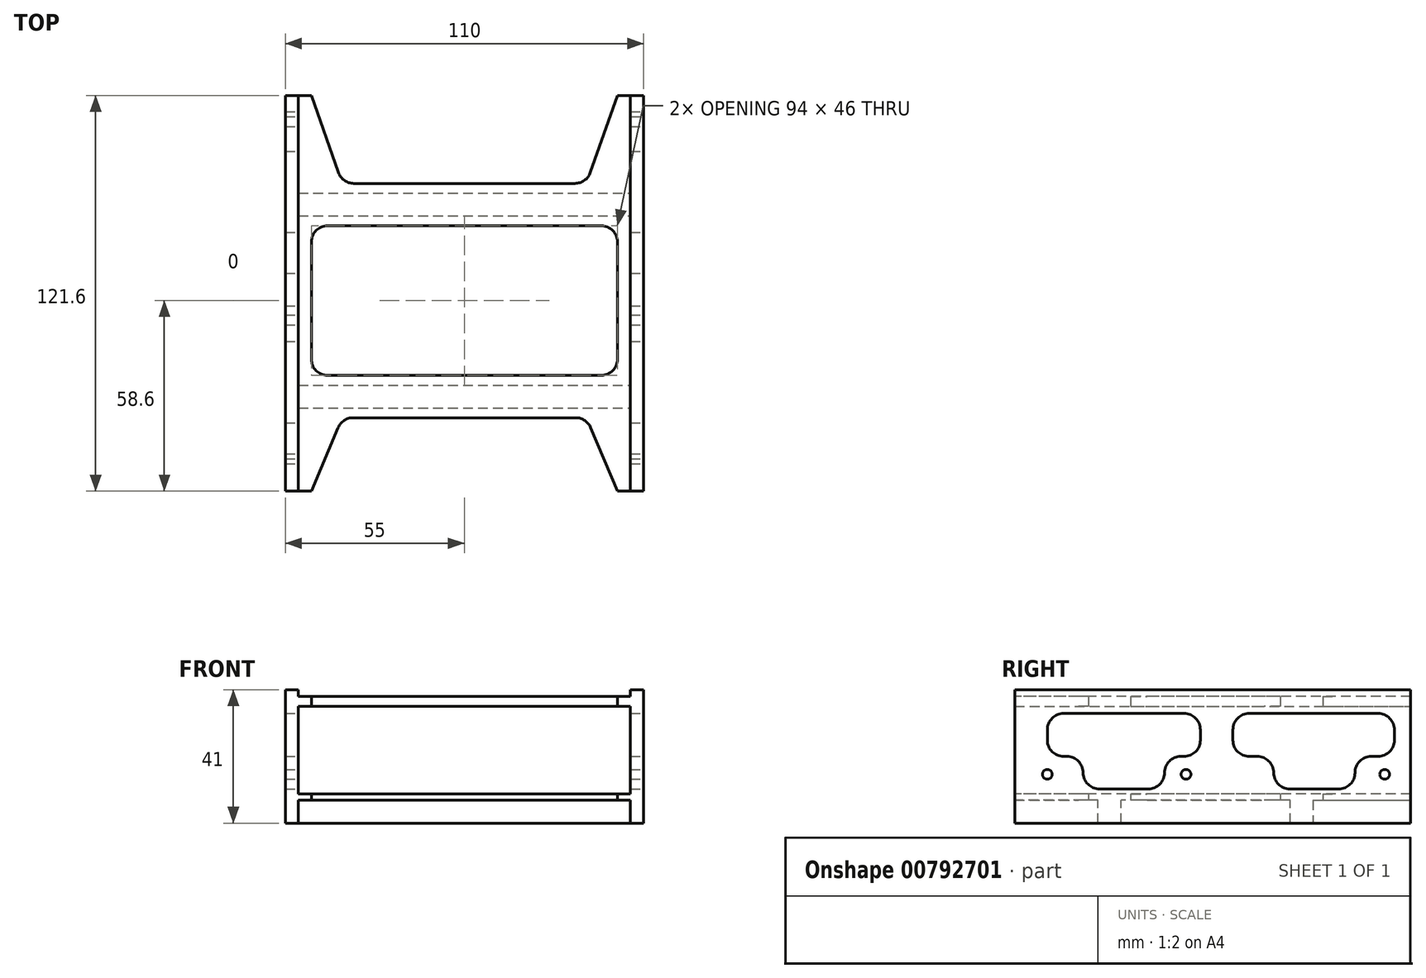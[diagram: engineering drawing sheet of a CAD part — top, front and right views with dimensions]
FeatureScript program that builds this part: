
annotation { "Feature Type Name" : "Feature", "Feature Type Description" : "" }
export const myFeature = defineFeature(function(context is Context, id is Id, definition is map)
    precondition{}
    {
        {
            var Q0;
            Q0=qCreatedBy(makeId("Right.planeOp"),FACE);
            var sketch = newSketch(context, id + "F0", { "sketchPlane" : qUnion([Q0])});
            skLineSegment(sketch, "E0.bottom", {"start": v(0, 0) * mm, "end": v(121.6, 0) * mm});
            skLineSegment(sketch, "E0.top", {"start": v(0, 41) * mm, "end": v(121.6, 41) * mm});
            skLineSegment(sketch, "E0.left", {"start": v(0, 0) * mm, "end": v(0, 41) * mm});
            skLineSegment(sketch, "E0.right", {"start": v(121.6, 0) * mm, "end": v(121.6, 41) * mm});
            skCircle(sketch, "E1", {"center": v(10, 15) * mm, "radius": 1.5 * mm});
            skCircle(sketch, "E2", {"center": v(52.6, 15) * mm, "radius": 1.5 * mm});
            skCircle(sketch, "E3", {"center": v(113.6, 15) * mm, "radius": 1.5 * mm});
            skLineSegment(sketch, "E4.bottom", {"start": v(-18.2, 35.2) * mm, "end": v(127.8, 35.2) * mm, "construction": true});
            skLineSegment(sketch, "E4.top", {"start": v(-18.2, 9.5) * mm, "end": v(127.8, 9.5) * mm, "construction": true});
            skLineSegment(sketch, "E4.left", {"start": v(-18.2, 35.2) * mm, "end": v(-18.2, 9.5) * mm, "construction": true});
            skLineSegment(sketch, "E4.right", {"start": v(127.8, 35.2) * mm, "end": v(127.8, 9.5) * mm, "construction": true});
            skSolve(sketch);
        }
        {
            var Q0;
            Q0=makeQuery(id+"F0.imprint","IMPRINT",FACE,{"disambiguationData":[TD([[makeQuery(id+"F0.imprint","IMPRINT",EDGE,{"derivedFrom":sQuery(id+"F0.wireOp",EDGE,"E0.bottom")}),1.0]])]});
            extrude(context, id + "F1", {"entities" : qUnion([Q0]), "oppositeDirection" : true, "depth" : 4 * mm, "offsetDistance" : 25 * mm});
        }
        {
            var Q0;
            Q0=makeQuery(id+"F1.opExtrude","CAP_FACE",FACE,{"disambiguationData":[OSD([sQuery(id+"F0.wireOp",EDGE,"E0.bottom"),sQuery(id+"F0.wireOp",EDGE,"E0.top"),sQuery(id+"F0.wireOp",EDGE,"E0.left"),sQuery(id+"F0.wireOp",EDGE,"E0.right"),sQuery(id+"F0.wireOp",EDGE,"E1"),sQuery(id+"F0.wireOp",EDGE,"E2"),sQuery(id+"F0.wireOp",EDGE,"E3")])],"isStart":false});
            var sketch = newSketch(context, id + "F2", { "sketchPlane" : qUnion([Q0])});
            skLineSegment(sketch, "E5.0", {"start": v(-127.8, 35.2) * mm, "end": v(-127.8, 9.5) * mm, "construction": true});
            skLineSegment(sketch, "E6.0", {"start": v(18.2, 35.2) * mm, "end": v(-127.8, 35.2) * mm, "construction": true});
            skLineSegment(sketch, "E7.0", {"start": v(18.2, 9.5) * mm, "end": v(-127.8, 9.5) * mm, "construction": true});
            skLineSegment(sketch, "E8.0", {"start": v(18.2, 35.2) * mm, "end": v(18.2, 9.5) * mm, "construction": true});
            skLineSegment(sketch, "E9.top", {"start": v(0, 35.95) * mm, "end": v(-121.6, 35.95) * mm});
            skLineSegment(sketch, "E9.left", {"start": v(0, 38.95) * mm, "end": v(0, 35.95) * mm});
            skLineSegment(sketch, "E9.right", {"start": v(-121.6, 38.95) * mm, "end": v(-121.6, 35.95) * mm});
            skLineSegment(sketch, "E10.top", {"start": v(-121.6, 9) * mm, "end": v(0, 9) * mm});
            skLineSegment(sketch, "E10.left", {"start": v(-121.6, 7) * mm, "end": v(-121.6, 9) * mm});
            skLineSegment(sketch, "E10.right", {"start": v(0, 7) * mm, "end": v(0, 9) * mm});
            skLineSegment(sketch, "E11", {"start": v(-91.6, 7) * mm, "end": v(-91.6, 0) * mm});
            skLineSegment(sketch, "E12", {"start": v(-91.6, 0) * mm, "end": v(-84.6, 0) * mm});
            skLineSegment(sketch, "E13", {"start": v(-84.6, 0) * mm, "end": v(-84.6, 7) * mm});
            skLineSegment(sketch, "E14", {"start": v(-32.6, 0) * mm, "end": v(-32.6, 7) * mm});
            skLineSegment(sketch, "E15", {"start": v(-25.6, 0) * mm, "end": v(-25.6, 7) * mm});
            skLineSegment(sketch, "E16", {"start": v(-32.6, 0) * mm, "end": v(-25.6, 0) * mm});
            skLineSegment(sketch, "E17.trimOffspring", {"start": v(-84.6, 7) * mm, "end": v(-32.6, 7) * mm});
            skLineSegment(sketch, "E18.trimOffspring", {"start": v(-25.6, 7) * mm, "end": v(0, 7) * mm});
            skLineSegment(sketch, "E19", {"start": v(-91.6, 7) * mm, "end": v(-121.6, 7) * mm});
            skLineSegment(sketch, "E20", {"start": v(-121.6, 38.95) * mm, "end": v(0, 38.95) * mm});
            skSolve(sketch);
        }
        {
            var Q0;
            Q0=makeQuery(id+"F2.imprint","IMPRINT",FACE,{"disambiguationData":[TD([[makeQuery(id+"F2.imprint","IMPRINT",EDGE,{"derivedFrom":sQuery(id+"F2.wireOp",EDGE,"E10.top")}),-1.0]])]});
            var Q1;
            Q1=makeQuery(id+"F2.imprint","IMPRINT",FACE,{"disambiguationData":[TD([[makeQuery(id+"F2.imprint","IMPRINT",EDGE,{"derivedFrom":sQuery(id+"F2.wireOp",EDGE,"E9.top")}),-1.0]])]});
            extrude(context, id + "F3", {"entities" : qUnion([Q0, Q1]), "operationType" : NewBodyOperationType.ADD, "depth" : 102 * mm, "offsetDistance" : 25 * mm});
        }
        {
            var Q0;
            Q0=makeQuery(id+"F3.opExtrude","SWEPT_FACE",FACE,{"disambiguationData":[OSD([sQuery(id+"F2.wireOp",EDGE,"E17.trimOffspring")])]});
            var sketch = newSketch(context, id + "F4", { "sketchPlane" : qUnion([Q0])});
            skLineSegment(sketch, "E21.0", {"start": v(-102, 0) * mm, "end": v(-8, 0) * mm});
            skLineSegment(sketch, "E22", {"start": v(-55, 0) * mm, "end": v(-55, -121.6) * mm, "construction": true});
            skLineSegment(sketch, "E23", {"start": v(-8, 0) * mm, "end": v(-16.21, -19.54) * mm});
            skLineSegment(sketch, "E24.MirrorCS", {"start": v(-102, 0) * mm, "end": v(-93.79, -19.54) * mm});
            skLineSegment(sketch, "E25", {"start": v(-89.18, -22.6) * mm, "end": v(-20.82, -22.6) * mm});
            skLineSegment(sketch, "E26", {"start": v(-8, -40.6) * mm, "end": v(-8, -76.6) * mm});
            skLineSegment(sketch, "E27.MirrorCS", {"start": v(-102, -40.6) * mm, "end": v(-102, -76.6) * mm});
            skLineSegment(sketch, "E28", {"start": v(-97, -35.6) * mm, "end": v(-13, -35.6) * mm});
            skLineSegment(sketch, "E29", {"start": v(-13, -81.6) * mm, "end": v(-97, -81.6) * mm});
            skPoint(sketch, "E30.visualSharp", {"position": v(-92.5, -22.6) * mm});
            skArc(sketch, "E30.filletArc", {"start": v(-93.79, -19.54) * mm, "mid": v(-91.94, -21.76) * mm, "end": v(-89.18, -22.6) * mm});
            skPoint(sketch, "E31.visualSharp", {"position": v(-17.5, -22.6) * mm});
            skArc(sketch, "E31.filletArc", {"start": v(-20.82, -22.6) * mm, "mid": v(-18.06, -21.76) * mm, "end": v(-16.21, -19.54) * mm});
            skPoint(sketch, "E32.visualSharp", {"position": v(-8, -35.6) * mm});
            skArc(sketch, "E32.filletArc", {"start": v(-8, -40.6) * mm, "mid": v(-9.46, -37.06) * mm, "end": v(-13, -35.6) * mm});
            skPoint(sketch, "E33.visualSharp", {"position": v(-102, -35.6) * mm});
            skArc(sketch, "E33.filletArc", {"start": v(-97, -35.6) * mm, "mid": v(-100.54, -37.06) * mm, "end": v(-102, -40.6) * mm});
            skPoint(sketch, "E34.visualSharp", {"position": v(-102, -81.6) * mm});
            skArc(sketch, "E34.filletArc", {"start": v(-102, -76.6) * mm, "mid": v(-100.54, -80.14) * mm, "end": v(-97, -81.6) * mm});
            skPoint(sketch, "E35.visualSharp", {"position": v(-8, -81.6) * mm});
            skArc(sketch, "E35.filletArc", {"start": v(-13, -81.6) * mm, "mid": v(-9.46, -80.14) * mm, "end": v(-8, -76.6) * mm});
            skPoint(sketch, "E36.orphan", {"position": v(-106, 0) * mm});
            skPoint(sketch, "E37.orphan", {"position": v(-4, 0) * mm});
            skLineSegment(sketch, "E38", {"start": v(-16.32, -97.94) * mm, "end": v(-8, -121.6) * mm});
            skLineSegment(sketch, "E39.0", {"start": v(-102, -121.6) * mm, "end": v(-8, -121.6) * mm});
            skLineSegment(sketch, "E40.MirrorCS", {"start": v(-93.68, -97.94) * mm, "end": v(-102, -121.6) * mm});
            skPoint(sketch, "E41.orphan", {"position": v(-106, -121.6) * mm});
            skPoint(sketch, "E42.orphan", {"position": v(-4, -121.6) * mm});
            skLineSegment(sketch, "E43", {"start": v(-88.96, -94.6) * mm, "end": v(-21.04, -94.6) * mm});
            skPoint(sketch, "E44.visualSharp", {"position": v(-92.5, -94.6) * mm});
            skArc(sketch, "E44.filletArc", {"start": v(-88.96, -94.6) * mm, "mid": v(-91.85, -95.52) * mm, "end": v(-93.68, -97.94) * mm});
            skPoint(sketch, "E45.visualSharp", {"position": v(-17.5, -94.6) * mm});
            skArc(sketch, "E45.filletArc", {"start": v(-16.32, -97.94) * mm, "mid": v(-18.15, -95.52) * mm, "end": v(-21.04, -94.6) * mm});
            skSolve(sketch);
        }
        {
            var Q0;
            Q0=makeQuery(id+"F4.imprint","IMPRINT",FACE,{"disambiguationData":[TD([[makeQuery(id+"F4.imprint","IMPRINT",EDGE,{"derivedFrom":sQuery(id+"F4.wireOp",EDGE,"E26")}),-1.0]])]});
            var Q1;
            Q1=makeQuery(id+"F4.imprint","IMPRINT",FACE,{"disambiguationData":[TD([[makeQuery(id+"F4.imprint","IMPRINT",EDGE,{"derivedFrom":sQuery(id+"F4.wireOp",EDGE,"E21.0")}),-1.0]])]});
            var Q2;
            Q2=makeQuery(id+"F4.imprint","IMPRINT",FACE,{"disambiguationData":[TD([[makeQuery(id+"F4.imprint","IMPRINT",EDGE,{"derivedFrom":sQuery(id+"F4.wireOp",EDGE,"E38")}),-1.0]])]});
            extrude(context, id + "F5", {"entities" : qUnion([Q0, Q1, Q2]), "operationType" : NewBodyOperationType.REMOVE, "endBound" : BoundingType.THROUGH_ALL, "oppositeDirection" : true, "depth" : 25 * mm, "offsetDistance" : 25 * mm});
        }
        {
            var Q0;
            Q0=makeQuery(id+"F3.opExtrude","CAP_FACE",FACE,{"disambiguationData":[OSD([sQuery(id+"F2.wireOp",EDGE,"E9.top"),sQuery(id+"F2.wireOp",EDGE,"E9.left"),sQuery(id+"F2.wireOp",EDGE,"E9.right"),sQuery(id+"F2.wireOp",EDGE,"E20")])],"isStart":false});
            var sketch = newSketch(context, id + "F6", { "sketchPlane" : qUnion([Q0])});
            skLineSegment(sketch, "E46.0", {"start": v(-121.6, 0) * mm, "end": v(-121.6, 41) * mm});
            skLineSegment(sketch, "E47.0", {"start": v(0, 41) * mm, "end": v(-121.6, 41) * mm});
            skLineSegment(sketch, "E48.0", {"start": v(0, 0) * mm, "end": v(-121.6, 0) * mm});
            skLineSegment(sketch, "E49.0", {"start": v(0, 0) * mm, "end": v(0, 41) * mm});
            skCircle(sketch, "E50.0", {"center": v(-113.6, 15) * mm, "radius": 1.5 * mm});
            skCircle(sketch, "E51.0", {"center": v(-52.6, 15) * mm, "radius": 1.5 * mm});
            skCircle(sketch, "E52.0", {"center": v(-10, 15) * mm, "radius": 1.5 * mm});
            skSolve(sketch);
        }
        {
            var Q0;
            {var subQ0=sQuery(id+"F6.wireOp",EDGE,"E48.0");Q0=makeQuery(id+"F6.imprint","IMPRINT",FACE,{"disambiguationData":[TD([[makeQuery(id+"F6.imprint","IMPRINT",EDGE,{"derivedFrom":subQ0}),-1.0]])]});}
            var Q1;
            {var subQ2=sQuery(id+"F6.wireOp",EDGE,"E47.0");Q1=makeQuery(id+"F6.imprint","IMPRINT",FACE,{"disambiguationData":[TD([[makeQuery(id+"F6.imprint","IMPRINT",EDGE,{"derivedFrom":subQ2}),1.0]])]});}
            var Q2;
            {var subQ1=makeQuery(id+"F3.opExtrude","CAP_EDGE",EDGE,{"disambiguationData":[OSD([sQuery(id+"F2.wireOp",EDGE,"E9.top")])],"isStart":false});Q2=makeQuery(id+"F6.imprint","IMPRINT",FACE,{"disambiguationData":[TD([[makeQuery(id+"F6.imprint","IMPRINT",EDGE,{"derivedFrom":subQ1}),-1.0]])]});}
            extrude(context, id + "F7", {"entities" : qUnion([Q0, Q1, Q2]), "operationType" : NewBodyOperationType.ADD, "depth" : 4 * mm, "offsetDistance" : 25 * mm});
        }
        {
            var Q0;
            Q0=qCreatedBy(makeId("Right.planeOp"),FACE);
            var sketch = newSketch(context, id + "F8", { "sketchPlane" : qUnion([Q0])});
            skLineSegment(sketch, "E53.bottom", {"start": v(15, 33.7) * mm, "end": v(52, 33.7) * mm});
            skLineSegment(sketch, "E53.top", {"start": v(15, 20.5) * mm, "end": v(16, 20.5) * mm});
            skLineSegment(sketch, "E53.left", {"start": v(10, 28.7) * mm, "end": v(10, 25.5) * mm});
            skLineSegment(sketch, "E53.right", {"start": v(57, 28.7) * mm, "end": v(57, 25.5) * mm});
            skLineSegment(sketch, "E54.top", {"start": v(26, 10.5) * mm, "end": v(41, 10.5) * mm});
            skLineSegment(sketch, "E54.left", {"start": v(21, 15.5) * mm, "end": v(21, 15.5) * mm});
            skLineSegment(sketch, "E54.right", {"start": v(46, 15.5) * mm, "end": v(46, 15.5) * mm});
            skLineSegment(sketch, "E55.bottom", {"start": v(72, 33.7) * mm, "end": v(111.6, 33.7) * mm});
            skLineSegment(sketch, "E55.top", {"start": v(72, 20.5) * mm, "end": v(74.5, 20.5) * mm});
            skLineSegment(sketch, "E55.left", {"start": v(67, 28.7) * mm, "end": v(67, 25.5) * mm});
            skLineSegment(sketch, "E55.right", {"start": v(116.6, 28.7) * mm, "end": v(116.6, 25.5) * mm});
            skLineSegment(sketch, "E56.top", {"start": v(84.5, 10.5) * mm, "end": v(99.5, 10.5) * mm});
            skLineSegment(sketch, "E56.left", {"start": v(79.5, 15.5) * mm, "end": v(79.5, 15.5) * mm});
            skLineSegment(sketch, "E56.right", {"start": v(104.5, 15.5) * mm, "end": v(104.5, 15.5) * mm});
            skLineSegment(sketch, "E57.trimOffspring", {"start": v(109.5, 20.5) * mm, "end": v(111.6, 20.5) * mm});
            skLineSegment(sketch, "E58.trimOffspring", {"start": v(51, 20.5) * mm, "end": v(52, 20.5) * mm});
            skPoint(sketch, "E59.visualSharp", {"position": v(46, 20.5) * mm});
            skArc(sketch, "E59.filletArc", {"start": v(51, 20.5) * mm, "mid": v(47.46, 19.04) * mm, "end": v(46, 15.5) * mm});
            skPoint(sketch, "E60.visualSharp", {"position": v(46, 10.5) * mm});
            skArc(sketch, "E60.filletArc", {"start": v(41, 10.5) * mm, "mid": v(44.54, 11.96) * mm, "end": v(46, 15.5) * mm});
            skPoint(sketch, "E61.visualSharp", {"position": v(21, 10.5) * mm});
            skArc(sketch, "E61.filletArc", {"start": v(21, 15.5) * mm, "mid": v(22.46, 11.96) * mm, "end": v(26, 10.5) * mm});
            skPoint(sketch, "E62.visualSharp", {"position": v(21, 20.5) * mm});
            skArc(sketch, "E62.filletArc", {"start": v(21, 15.5) * mm, "mid": v(19.54, 19.04) * mm, "end": v(16, 20.5) * mm});
            skPoint(sketch, "E63.visualSharp", {"position": v(10, 20.5) * mm});
            skArc(sketch, "E63.filletArc", {"start": v(10, 25.5) * mm, "mid": v(11.46, 21.96) * mm, "end": v(15, 20.5) * mm});
            skPoint(sketch, "E64.visualSharp", {"position": v(10, 33.7) * mm});
            skArc(sketch, "E64.filletArc", {"start": v(15, 33.7) * mm, "mid": v(11.46, 32.24) * mm, "end": v(10, 28.7) * mm});
            skPoint(sketch, "E65.visualSharp", {"position": v(57, 33.7) * mm});
            skArc(sketch, "E65.filletArc", {"start": v(57, 28.7) * mm, "mid": v(55.54, 32.24) * mm, "end": v(52, 33.7) * mm});
            skPoint(sketch, "E66.visualSharp", {"position": v(67, 33.7) * mm});
            skArc(sketch, "E66.filletArc", {"start": v(72, 33.7) * mm, "mid": v(68.46, 32.24) * mm, "end": v(67, 28.7) * mm});
            skPoint(sketch, "E67.visualSharp", {"position": v(67, 20.5) * mm});
            skArc(sketch, "E67.filletArc", {"start": v(67, 25.5) * mm, "mid": v(68.46, 21.96) * mm, "end": v(72, 20.5) * mm});
            skPoint(sketch, "E68.visualSharp", {"position": v(79.5, 10.5) * mm});
            skArc(sketch, "E68.filletArc", {"start": v(79.5, 15.5) * mm, "mid": v(80.96, 11.96) * mm, "end": v(84.5, 10.5) * mm});
            skPoint(sketch, "E69.visualSharp", {"position": v(104.5, 10.5) * mm});
            skArc(sketch, "E69.filletArc", {"start": v(99.5, 10.5) * mm, "mid": v(103.04, 11.96) * mm, "end": v(104.5, 15.5) * mm});
            skPoint(sketch, "E70.visualSharp", {"position": v(104.5, 20.5) * mm});
            skArc(sketch, "E70.filletArc", {"start": v(109.5, 20.5) * mm, "mid": v(105.96, 19.04) * mm, "end": v(104.5, 15.5) * mm});
            skPoint(sketch, "E71.visualSharp", {"position": v(116.6, 20.5) * mm});
            skArc(sketch, "E71.filletArc", {"start": v(111.6, 20.5) * mm, "mid": v(115.14, 21.96) * mm, "end": v(116.6, 25.5) * mm});
            skPoint(sketch, "E72.visualSharp", {"position": v(116.6, 33.7) * mm});
            skArc(sketch, "E72.filletArc", {"start": v(116.6, 28.7) * mm, "mid": v(115.14, 32.24) * mm, "end": v(111.6, 33.7) * mm});
            skPoint(sketch, "E73.visualSharp", {"position": v(57, 20.5) * mm});
            skArc(sketch, "E73.filletArc", {"start": v(52, 20.5) * mm, "mid": v(55.54, 21.96) * mm, "end": v(57, 25.5) * mm});
            skPoint(sketch, "E74.visualSharp", {"position": v(79.5, 20.5) * mm});
            skArc(sketch, "E74.filletArc", {"start": v(79.5, 15.5) * mm, "mid": v(78.04, 19.04) * mm, "end": v(74.5, 20.5) * mm});
            skSolve(sketch);
        }
        {
            var Q0;
            Q0 = qSketchRegion(id + "F8", true);
            extrude(context, id + "F9", {"entities" : qUnion([Q0]), "operationType" : NewBodyOperationType.REMOVE, "endBound" : BoundingType.THROUGH_ALL, "oppositeDirection" : true, "depth" : 25 * mm, "offsetDistance" : 25 * mm});
        }
    });
